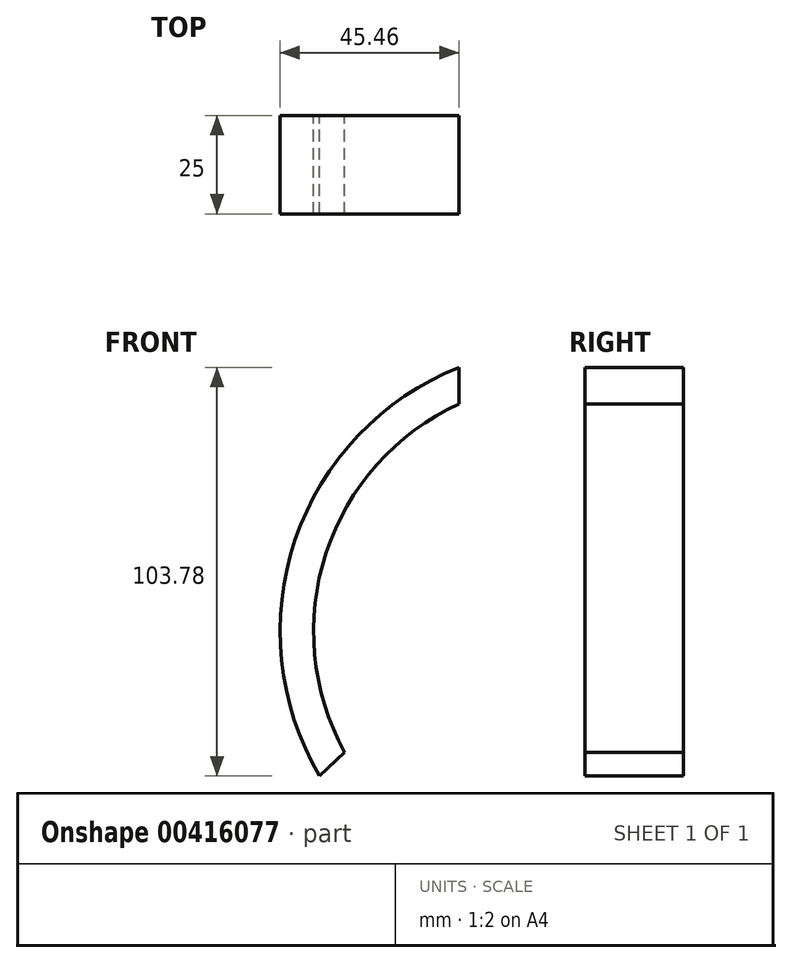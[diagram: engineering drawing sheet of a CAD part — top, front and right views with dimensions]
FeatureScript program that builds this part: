
annotation { "Feature Type Name" : "Feature", "Feature Type Description" : "" }
export const myFeature = defineFeature(function(context is Context, id is Id, definition is map)
    precondition{}
    {
        {
            var Q0;
            Q0=qCreatedBy(makeId("Front.planeOp"),FACE);
            var sketch = newSketch(context, id + "F0", { "sketchPlane" : qUnion([Q0])});
            skArc(sketch, "E0", {"start": v(-26.66, 67.01) * mm, "mid": v(-68.27, 23.27) * mm, "end": v(-62.05, -36.77) * mm});
            skArc(sketch, "E1", {"start": v(-26.66, 57.75) * mm, "mid": v(-60.44, 19.83) * mm, "end": v(-55.7, -30.73) * mm});
            skLineSegment(sketch, "E2", {"start": v(-26.66, 67.01) * mm, "end": v(-26.66, 57.75) * mm});
            skLineSegment(sketch, "E3", {"start": v(-62.05, -36.77) * mm, "end": v(-55.7, -30.73) * mm});
            skSolve(sketch);
        }
        {
            var Q0;
            Q0 = qSketchRegion(id + "F0", true);
            extrude(context, id + "F1", {"entities" : qUnion([Q0]), "depth" : 25 * mm});
        }
    });
